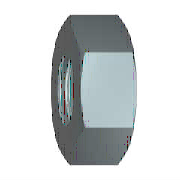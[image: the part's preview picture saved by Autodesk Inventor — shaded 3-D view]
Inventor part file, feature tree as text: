
AUTODESK INVENTOR PART (.ipt)
format: ipt  version: 2013 (Build 170138000, 138)  size: 171,008 bytes
history: native  units: mm (DEFAULTED — no unit token found)
features: sketch x3, chamfer x1, hole x1, other x1, plane x1
ambient origin geometry x7: Origin, YZ Plane, XZ Plane, X Axis, Y Axis, Z Axis, Center Point
bodies: Solid1 (feature_tree), Body (feature_tree)
feature tree (7):
  chamfer  "Chamfer1"  Distance=4.363323mm
  hole  "Thread"  [1 undecoded]
  other  "Work Axis1"
  plane  "Work Plane1"
  sketch  "Sketch1"  dims[d0=6.350853mm]
  sketch  "Sketch2"  dims[d1=2.4mm]
  sketch  "Sketch3"  dims[d2=0.0mm d3=4.363323mm d4=4.363323mm d5=5.5mm d6=5.5mm d7=90.0deg d25=2.459mm d26=6.0mm d27=4.0mm d28=2.0mm d29=14.3117mm d30=8.0mm d31=20.594885mm d8=0.270633mm d9=30.0deg d10=0.270633mm d11=30.0deg d13=0.0mm d14=0.0mm d39=0.0mm d40=0.270633mm d41=0.270633mm d42=0.0mm]
note: 1 required parameter value undecoded (feature->parameter linkage not recoverable at this tier; creation-order binding heuristic only, values carry confidence <= 0.55)
